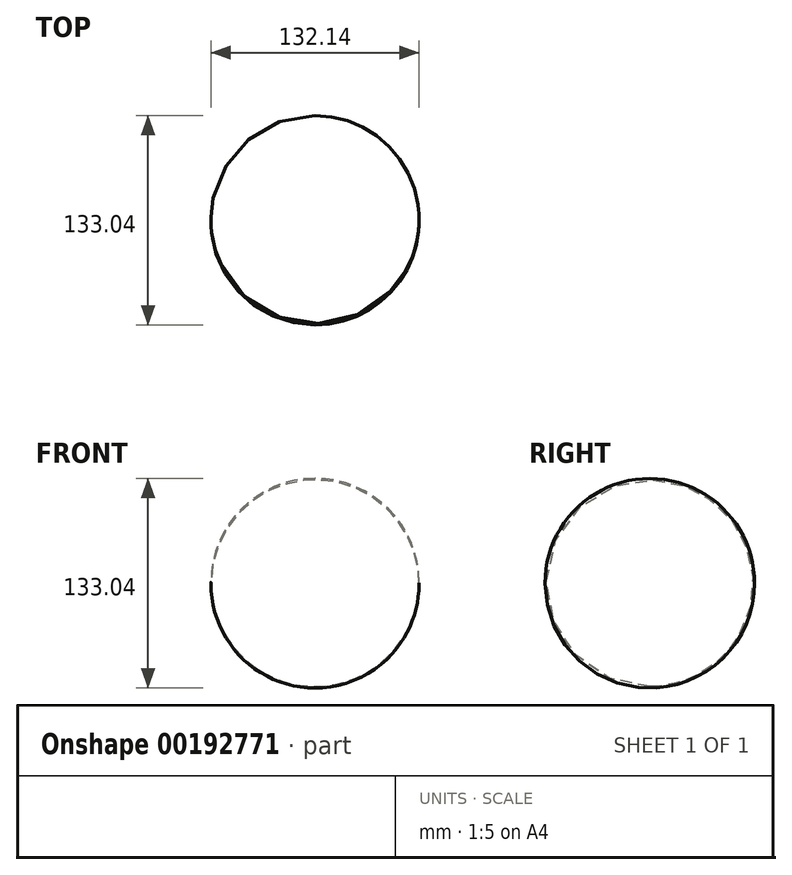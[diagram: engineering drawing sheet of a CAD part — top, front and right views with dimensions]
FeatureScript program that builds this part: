
annotation { "Feature Type Name" : "Feature", "Feature Type Description" : "" }
export const myFeature = defineFeature(function(context is Context, id is Id, definition is map)
    precondition{}
    {
        {
            var Q0;
            Q0=qCreatedBy(makeId("Front.planeOp"),FACE);
            var sketch = newSketch(context, id + "F0", { "sketchPlane" : qUnion([Q0])});
            skArc(sketch, "E0", {"start": v(66.07, 0.24) * mm, "mid": v(0.21, 66.07) * mm, "end": v(-66.07, 0.66) * mm});
            skLineSegment(sketch, "E1", {"start": v(-66.07, 0.66) * mm, "end": v(66.07, 0.24) * mm});
            skSolve(sketch);
        }
        {
            var Q0;
            Q0 = qSketchRegion(id + "F0", true);
            var Q1;
            Q1=sQuery(id+"F0.wireOp",EDGE,"E1");
            revolve(context, id + "F1", {"entities" : qUnion([Q0]), "axis" : qUnion([Q1]), "revolveType" : RevolveType.FULL});
        }
    });
